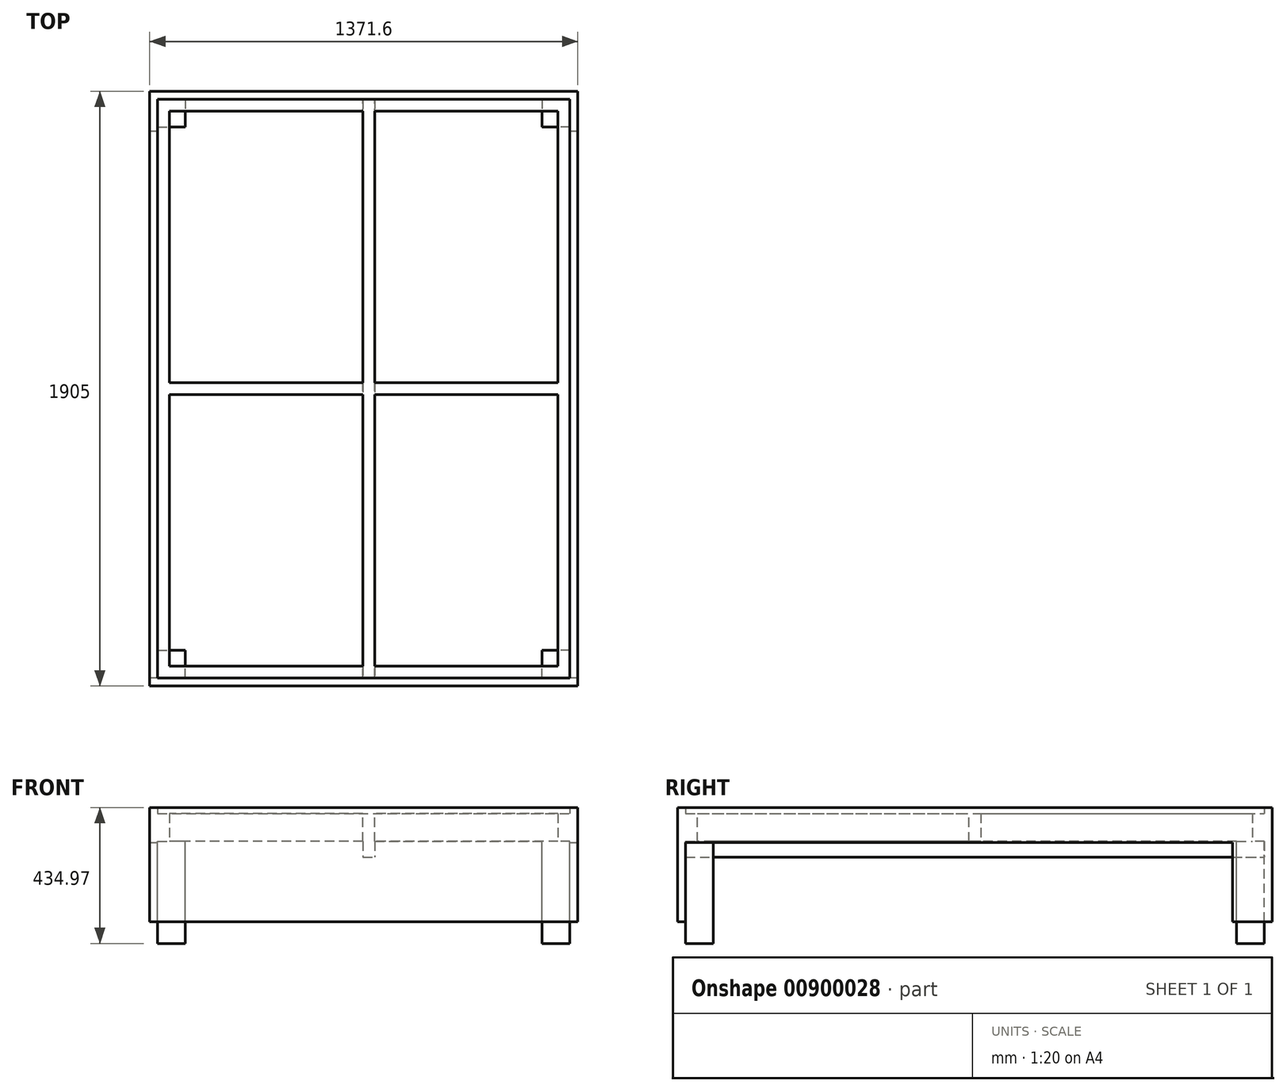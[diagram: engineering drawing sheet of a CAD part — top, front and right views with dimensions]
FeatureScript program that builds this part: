
annotation { "Feature Type Name" : "Feature", "Feature Type Description" : "" }
export const myFeature = defineFeature(function(context is Context, id is Id, definition is map)
    precondition{}
    {
        {
            var Q0;
            Q0=qCreatedBy(makeId("Top.planeOp"),FACE);
            var sketch = newSketch(context, id + "F0", { "sketchPlane" : qUnion([Q0])});
            skLineSegment(sketch, "E0.bottom", {"start": v(685.8, 952.5) * mm, "end": v(-685.8, 952.5) * mm});
            skLineSegment(sketch, "E0.top", {"start": v(685.8, -952.5) * mm, "end": v(-685.8, -952.5) * mm});
            skLineSegment(sketch, "E0.left", {"start": v(685.8, 952.5) * mm, "end": v(685.8, -952.5) * mm});
            skLineSegment(sketch, "E0.right", {"start": v(-685.8, 952.5) * mm, "end": v(-685.8, -952.5) * mm});
            skPoint(sketch, "E0.middle", {"position": v(0, 0) * mm});
            skLineSegment(sketch, "E1.bottom", {"start": v(660.4, 927.1) * mm, "end": v(-660.4, 927.1) * mm});
            skLineSegment(sketch, "E1.top", {"start": v(660.4, -927.1) * mm, "end": v(-660.4, -927.1) * mm});
            skLineSegment(sketch, "E1.left", {"start": v(660.4, 927.1) * mm, "end": v(660.4, -927.1) * mm});
            skLineSegment(sketch, "E1.right", {"start": v(-660.4, 927.1) * mm, "end": v(-660.4, -927.1) * mm});
            skSolve(sketch);
        }
        {
            var Q0;
            Q0=makeQuery(id+"F0.imprint","IMPRINT",FACE,{"disambiguationData":[TD([[makeQuery(id+"F0.imprint","IMPRINT",EDGE,{"derivedFrom":sQuery(id+"F0.wireOp",EDGE,"E0.bottom")}),1.0]])]});
            extrude(context, id + "F1", {"entities" : qUnion([Q0]), "depth" : 365.12 * mm, "offsetDistance" : 25.4 * mm});
        }
        {
            var Q0;
            Q0=makeQuery(id+"F1.opExtrude","SWEPT_FACE",FACE,{"disambiguationData":[OSD([sQuery(id+"F0.wireOp",EDGE,"E1.bottom")])]});
            var sketch = newSketch(context, id + "F2", { "sketchPlane" : qUnion([Q0])});
            skLineSegment(sketch, "E2.bottom", {"start": v(-3.18, 346.08) * mm, "end": v(34.92, 346.08) * mm});
            skLineSegment(sketch, "E2.top", {"start": v(-3.18, 206.38) * mm, "end": v(34.92, 206.38) * mm});
            skLineSegment(sketch, "E2.left", {"start": v(-3.18, 346.08) * mm, "end": v(-3.18, 206.38) * mm});
            skLineSegment(sketch, "E2.right", {"start": v(34.92, 346.08) * mm, "end": v(34.92, 206.38) * mm});
            skSolve(sketch);
        }
        {
            var Q0;
            Q0 = qSketchRegion(id + "F2", true);
            extrude(context, id + "F3", {"entities" : qUnion([Q0]), "operationType" : NewBodyOperationType.ADD, "endBound" : BoundingType.UP_TO_NEXT, "depth" : 25.4 * mm, "offsetDistance" : 25.4 * mm});
        }
        {
            var Q0;
            Q0=makeQuery(id+"F1.opExtrude","SWEPT_FACE",FACE,{"disambiguationData":[OSD([sQuery(id+"F0.wireOp",EDGE,"E1.right")])]});
            var sketch = newSketch(context, id + "F4", { "sketchPlane" : qUnion([Q0])});
            skLineSegment(sketch, "E3.bottom", {"start": v(-927.1, 346.08) * mm, "end": v(927.1, 346.08) * mm});
            skLineSegment(sketch, "E3.top", {"start": v(-927.1, 257.18) * mm, "end": v(927.1, 257.18) * mm});
            skLineSegment(sketch, "E3.left", {"start": v(-927.1, 346.08) * mm, "end": v(-927.1, 257.18) * mm});
            skLineSegment(sketch, "E3.right", {"start": v(927.1, 346.08) * mm, "end": v(927.1, 257.18) * mm});
            skSolve(sketch);
        }
        {
            var Q0;
            Q0 = qSketchRegion(id + "F4", true);
            extrude(context, id + "F5", {"entities" : qUnion([Q0]), "operationType" : NewBodyOperationType.ADD, "depth" : 38.1 * mm, "offsetDistance" : 25.4 * mm});
        }
        {
            var Q0;
            Q0=makeQuery(id+"F1.opExtrude","SWEPT_FACE",FACE,{"disambiguationData":[OSD([sQuery(id+"F0.wireOp",EDGE,"E1.left")])]});
            var sketch = newSketch(context, id + "F6", { "sketchPlane" : qUnion([Q0])});
            skLineSegment(sketch, "E4.bottom", {"start": v(-927.1, 346.08) * mm, "end": v(927.1, 346.08) * mm});
            skLineSegment(sketch, "E4.top", {"start": v(-927.1, 257.18) * mm, "end": v(927.1, 257.18) * mm});
            skLineSegment(sketch, "E4.left", {"start": v(-927.1, 346.08) * mm, "end": v(-927.1, 257.18) * mm});
            skLineSegment(sketch, "E4.right", {"start": v(927.1, 346.08) * mm, "end": v(927.1, 257.18) * mm});
            skSolve(sketch);
        }
        {
            var Q0;
            Q0 = qSketchRegion(id + "F6", true);
            extrude(context, id + "F7", {"entities" : qUnion([Q0]), "operationType" : NewBodyOperationType.ADD, "depth" : 38.1 * mm, "offsetDistance" : 25.4 * mm});
        }
        {
            var Q0;
            Q0=makeQuery(id+"F1.opExtrude","SWEPT_FACE",FACE,{"disambiguationData":[OSD([sQuery(id+"F0.wireOp",EDGE,"E0.left")])]});
            var sketch = newSketch(context, id + "F8", { "sketchPlane" : qUnion([Q0])});
            skLineSegment(sketch, "E5.bottom", {"start": v(-927.1, 0) * mm, "end": v(825.5, 0) * mm});
            skLineSegment(sketch, "E5.top", {"start": v(-927.1, 254) * mm, "end": v(825.5, 254) * mm});
            skLineSegment(sketch, "E5.left", {"start": v(-927.1, 0) * mm, "end": v(-927.1, 254) * mm});
            skLineSegment(sketch, "E5.right", {"start": v(825.5, 0) * mm, "end": v(825.5, 254) * mm});
            skSolve(sketch);
        }
        {
            var Q0;
            Q0 = qSketchRegion(id + "F8", true);
            extrude(context, id + "F9", {"entities" : qUnion([Q0]), "operationType" : NewBodyOperationType.REMOVE, "endBound" : BoundingType.THROUGH_ALL, "oppositeDirection" : true, "depth" : 25.4 * mm, "offsetDistance" : 25.4 * mm});
        }
        {
            var Q0;
            Q0=makeQuery(id+"F9.boolean.opBoolean","COPY",FACE,{"disambiguationData":[TD([makeQuery(id+"F3.opExtrude","SWEPT_FACE",FACE,{"disambiguationData":[OSD([sQuery(id+"F2.wireOp",EDGE,"E2.top")])]})])],"derivedFrom":makeQuery(id+"F9.opExtrude","SWEPT_FACE",FACE,{"disambiguationData":[OSD([sQuery(id+"F8.wireOp",EDGE,"E5.right")])]})});
            extrude(context, id + "F10", {"entities" : qUnion([Q0]), "operationType" : NewBodyOperationType.ADD, "endBound" : BoundingType.UP_TO_NEXT, "depth" : 25.4 * mm, "offsetDistance" : 25.4 * mm});
        }
        {
            var Q0;
            Q0=makeQuery(id+"F5.opExtrude","CAP_FACE",FACE,{"disambiguationData":[OSD([sQuery(id+"F4.wireOp",EDGE,"E3.bottom"),sQuery(id+"F4.wireOp",EDGE,"E3.top"),sQuery(id+"F4.wireOp",EDGE,"E3.left"),sQuery(id+"F4.wireOp",EDGE,"E3.right")])],"isStart":false});
            var sketch = newSketch(context, id + "F11", { "sketchPlane" : qUnion([Q0])});
            skLineSegment(sketch, "E6.bottom", {"start": v(927.1, 346.08) * mm, "end": v(889, 346.08) * mm});
            skLineSegment(sketch, "E6.top", {"start": v(927.1, 257.18) * mm, "end": v(889, 257.18) * mm});
            skLineSegment(sketch, "E6.left", {"start": v(927.1, 346.08) * mm, "end": v(927.1, 257.18) * mm});
            skLineSegment(sketch, "E6.right", {"start": v(889, 346.08) * mm, "end": v(889, 257.18) * mm});
            skSolve(sketch);
        }
        {
            var Q0;
            Q0 = qSketchRegion(id + "F11", true);
            extrude(context, id + "F12", {"entities" : qUnion([Q0]), "operationType" : NewBodyOperationType.ADD, "depth" : 1270 * mm, "offsetDistance" : 25.4 * mm});
        }
        {
            var Q0;
            Q0=makeQuery(id+"F5.opExtrude","CAP_FACE",FACE,{"disambiguationData":[OSD([sQuery(id+"F4.wireOp",EDGE,"E3.bottom"),sQuery(id+"F4.wireOp",EDGE,"E3.top"),sQuery(id+"F4.wireOp",EDGE,"E3.left"),sQuery(id+"F4.wireOp",EDGE,"E3.right")])],"isStart":false});
            var sketch = newSketch(context, id + "F13", { "sketchPlane" : qUnion([Q0])});
            skLineSegment(sketch, "E7.bottom", {"start": v(-927.1, 346.08) * mm, "end": v(-889, 346.08) * mm});
            skLineSegment(sketch, "E7.top", {"start": v(-927.1, 257.18) * mm, "end": v(-889, 257.18) * mm});
            skLineSegment(sketch, "E7.left", {"start": v(-927.1, 346.08) * mm, "end": v(-927.1, 257.18) * mm});
            skLineSegment(sketch, "E7.right", {"start": v(-889, 346.08) * mm, "end": v(-889, 257.18) * mm});
            skSolve(sketch);
        }
        {
            var Q0;
            Q0 = qSketchRegion(id + "F13", true);
            extrude(context, id + "F14", {"entities" : qUnion([Q0]), "operationType" : NewBodyOperationType.ADD, "depth" : 1270 * mm, "offsetDistance" : 25.4 * mm});
        }
        {
            var Q0;
            Q0=makeQuery(id+"F5.opExtrude","CAP_FACE",FACE,{"disambiguationData":[OSD([sQuery(id+"F4.wireOp",EDGE,"E3.bottom"),sQuery(id+"F4.wireOp",EDGE,"E3.top"),sQuery(id+"F4.wireOp",EDGE,"E3.left"),sQuery(id+"F4.wireOp",EDGE,"E3.right")])],"isStart":false});
            var sketch = newSketch(context, id + "F15", { "sketchPlane" : qUnion([Q0])});
            skLineSegment(sketch, "E8.bottom", {"start": v(-19.05, 346.08) * mm, "end": v(19.05, 346.08) * mm});
            skLineSegment(sketch, "E8.top", {"start": v(-19.05, 257.18) * mm, "end": v(19.05, 257.18) * mm});
            skLineSegment(sketch, "E8.left", {"start": v(-19.05, 346.08) * mm, "end": v(-19.05, 257.18) * mm});
            skLineSegment(sketch, "E8.right", {"start": v(19.05, 346.08) * mm, "end": v(19.05, 257.18) * mm});
            skSolve(sketch);
        }
        {
            var Q0;
            Q0 = qSketchRegion(id + "F15", true);
            extrude(context, id + "F16", {"entities" : qUnion([Q0]), "operationType" : NewBodyOperationType.ADD, "depth" : 1270 * mm, "offsetDistance" : 25.4 * mm});
        }
        {
            var Q0;
            Q0=makeQuery(id+"F16.boolean.opBoolean","MERGE",FACE,{"derivedFrom":[makeQuery(id+"F14.boolean.opBoolean","MERGE",FACE,{"derivedFrom":[makeQuery(id+"F12.boolean.opBoolean","MERGE",FACE,{"derivedFrom":[makeQuery(id+"F5.opExtrude","SWEPT_FACE",FACE,{"disambiguationData":[OSD([sQuery(id+"F4.wireOp",EDGE,"E3.top")])]}),makeQuery(id+"F12.opExtrude","SWEPT_FACE",FACE,{"disambiguationData":[OSD([sQuery(id+"F11.wireOp",EDGE,"E6.top")])]})]}),makeQuery(id+"F14.opExtrude","SWEPT_FACE",FACE,{"disambiguationData":[OSD([sQuery(id+"F13.wireOp",EDGE,"E7.top")])]})]}),makeQuery(id+"F16.opExtrude","SWEPT_FACE",FACE,{"disambiguationData":[OSD([sQuery(id+"F15.wireOp",EDGE,"E8.top")])]})]});
            var sketch = newSketch(context, id + "F17", { "sketchPlane" : qUnion([Q0])});
            skLineSegment(sketch, "E9.bottom", {"start": v(-660.4, 927.1) * mm, "end": v(-571.5, 927.1) * mm});
            skLineSegment(sketch, "E9.top", {"start": v(-660.4, 838.2) * mm, "end": v(-571.5, 838.2) * mm});
            skLineSegment(sketch, "E9.left", {"start": v(-660.4, 927.1) * mm, "end": v(-660.4, 838.2) * mm});
            skLineSegment(sketch, "E9.right", {"start": v(-571.5, 927.1) * mm, "end": v(-571.5, 838.2) * mm});
            skSolve(sketch);
        }
        {
            var Q0;
            Q0 = qSketchRegion(id + "F17", true);
            extrude(context, id + "F18", {"entities" : qUnion([Q0]), "operationType" : NewBodyOperationType.ADD, "depth" : 327.02 * mm, "offsetDistance" : 25.4 * mm});
        }
        {
            var Q0;
            Q0=makeQuery(id+"F16.boolean.opBoolean","MERGE",FACE,{"derivedFrom":[makeQuery(id+"F14.boolean.opBoolean","MERGE",FACE,{"derivedFrom":[makeQuery(id+"F12.boolean.opBoolean","MERGE",FACE,{"derivedFrom":[makeQuery(id+"F7.opExtrude","SWEPT_FACE",FACE,{"disambiguationData":[OSD([sQuery(id+"F6.wireOp",EDGE,"E4.top")])]}),makeQuery(id+"F12.opExtrude","SWEPT_FACE",FACE,{"disambiguationData":[OSD([sQuery(id+"F11.wireOp",EDGE,"E6.top")])]})]}),makeQuery(id+"F14.opExtrude","SWEPT_FACE",FACE,{"disambiguationData":[OSD([sQuery(id+"F13.wireOp",EDGE,"E7.top")])]})]}),makeQuery(id+"F16.opExtrude","SWEPT_FACE",FACE,{"disambiguationData":[OSD([sQuery(id+"F15.wireOp",EDGE,"E8.top")])]})]});
            var sketch = newSketch(context, id + "F19", { "sketchPlane" : qUnion([Q0])});
            skLineSegment(sketch, "E10.bottom", {"start": v(660.4, 927.1) * mm, "end": v(571.5, 927.1) * mm});
            skLineSegment(sketch, "E10.top", {"start": v(660.4, 838.2) * mm, "end": v(571.5, 838.2) * mm});
            skLineSegment(sketch, "E10.left", {"start": v(660.4, 927.1) * mm, "end": v(660.4, 838.2) * mm});
            skLineSegment(sketch, "E10.right", {"start": v(571.5, 927.1) * mm, "end": v(571.5, 838.2) * mm});
            skSolve(sketch);
        }
        {
            var Q0;
            Q0 = qSketchRegion(id + "F19", true);
            extrude(context, id + "F20", {"entities" : qUnion([Q0]), "operationType" : NewBodyOperationType.ADD, "depth" : 327.02 * mm, "offsetDistance" : 25.4 * mm});
        }
        {
            var Q0;
            {var subQ1=sQuery(id+"F4.wireOp",EDGE,"E3.top");Q0=makeQuery(id+"F18.boolean.opBoolean","SPLIT",FACE,{"disambiguationData":[TD([makeQuery(id+"F1.opExtrude","SWEPT_FACE",FACE,{"disambiguationData":[OSD([sQuery(id+"F0.wireOp",EDGE,"E1.bottom")])]})])],"derivedFrom":makeQuery(id+"F16.boolean.opBoolean","MERGE",FACE,{"derivedFrom":[makeQuery(id+"F14.boolean.opBoolean","MERGE",FACE,{"derivedFrom":[makeQuery(id+"F12.boolean.opBoolean","MERGE",FACE,{"derivedFrom":[makeQuery(id+"F5.opExtrude","SWEPT_FACE",FACE,{"disambiguationData":[OSD([subQ1])]}),makeQuery(id+"F12.opExtrude","SWEPT_FACE",FACE,{"disambiguationData":[OSD([sQuery(id+"F11.wireOp",EDGE,"E6.top")])]})]}),makeQuery(id+"F14.opExtrude","SWEPT_FACE",FACE,{"disambiguationData":[OSD([sQuery(id+"F13.wireOp",EDGE,"E7.top")])]})]}),makeQuery(id+"F16.opExtrude","SWEPT_FACE",FACE,{"disambiguationData":[OSD([sQuery(id+"F15.wireOp",EDGE,"E8.top")])]})]})});}
            var sketch = newSketch(context, id + "F21", { "sketchPlane" : qUnion([Q0])});
            skLineSegment(sketch, "E11.bottom", {"start": v(-660.4, -927.1) * mm, "end": v(-571.5, -927.1) * mm});
            skLineSegment(sketch, "E11.top", {"start": v(-660.4, -838.2) * mm, "end": v(-571.5, -838.2) * mm});
            skLineSegment(sketch, "E11.left", {"start": v(-660.4, -927.1) * mm, "end": v(-660.4, -838.2) * mm});
            skLineSegment(sketch, "E11.right", {"start": v(-571.5, -927.1) * mm, "end": v(-571.5, -838.2) * mm});
            skSolve(sketch);
        }
        {
            var Q0;
            Q0 = qSketchRegion(id + "F21", true);
            extrude(context, id + "F22", {"entities" : qUnion([Q0]), "operationType" : NewBodyOperationType.ADD, "depth" : 327.02 * mm, "offsetDistance" : 25.4 * mm});
        }
        {
            var Q0;
            {var subQ0=sQuery(id+"F6.wireOp",EDGE,"E4.top");Q0=makeQuery(id+"F20.boolean.opBoolean","SPLIT",FACE,{"disambiguationData":[TD([makeQuery(id+"F1.opExtrude","SWEPT_FACE",FACE,{"disambiguationData":[OSD([sQuery(id+"F0.wireOp",EDGE,"E1.bottom")])]})])],"derivedFrom":makeQuery(id+"F16.boolean.opBoolean","MERGE",FACE,{"derivedFrom":[makeQuery(id+"F14.boolean.opBoolean","MERGE",FACE,{"derivedFrom":[makeQuery(id+"F12.boolean.opBoolean","MERGE",FACE,{"derivedFrom":[makeQuery(id+"F7.opExtrude","SWEPT_FACE",FACE,{"disambiguationData":[OSD([subQ0])]}),makeQuery(id+"F12.opExtrude","SWEPT_FACE",FACE,{"disambiguationData":[OSD([sQuery(id+"F11.wireOp",EDGE,"E6.top")])]})]}),makeQuery(id+"F14.opExtrude","SWEPT_FACE",FACE,{"disambiguationData":[OSD([sQuery(id+"F13.wireOp",EDGE,"E7.top")])]})]}),makeQuery(id+"F16.opExtrude","SWEPT_FACE",FACE,{"disambiguationData":[OSD([sQuery(id+"F15.wireOp",EDGE,"E8.top")])]})]})});}
            var sketch = newSketch(context, id + "F23", { "sketchPlane" : qUnion([Q0])});
            skLineSegment(sketch, "E12.bottom", {"start": v(660.4, -927.1) * mm, "end": v(571.5, -927.1) * mm});
            skLineSegment(sketch, "E12.top", {"start": v(660.4, -838.2) * mm, "end": v(571.5, -838.2) * mm});
            skLineSegment(sketch, "E12.left", {"start": v(660.4, -927.1) * mm, "end": v(660.4, -838.2) * mm});
            skLineSegment(sketch, "E12.right", {"start": v(571.5, -927.1) * mm, "end": v(571.5, -838.2) * mm});
            skSolve(sketch);
        }
        {
            var Q0;
            Q0 = qSketchRegion(id + "F23", true);
            extrude(context, id + "F24", {"entities" : qUnion([Q0]), "operationType" : NewBodyOperationType.ADD, "depth" : 327.02 * mm, "offsetDistance" : 25.4 * mm});
        }
    });
